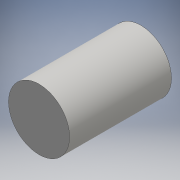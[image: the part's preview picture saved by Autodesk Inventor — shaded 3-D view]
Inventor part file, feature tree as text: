
AUTODESK INVENTOR PART (.ipt)
format: ipt  version: 2016 (Build 200138000, 138)  size: 86,016 bytes
history: native  units: mm
features: extrude x1, sketch x1
ambient origin geometry x8: Origin, YZ Plane, XZ Plane, XY Plane, X Axis, Y Axis, Z Axis, Center Point
bodies: Solid1 (feature_tree)
feature tree (2):
  extrude  "Extrusion1"  Depth=20.0mm TaperAngle=0.0deg
  sketch  "Sketch1"  dims[d0=12.0mm d1=20.0mm d2=0.0mm]
